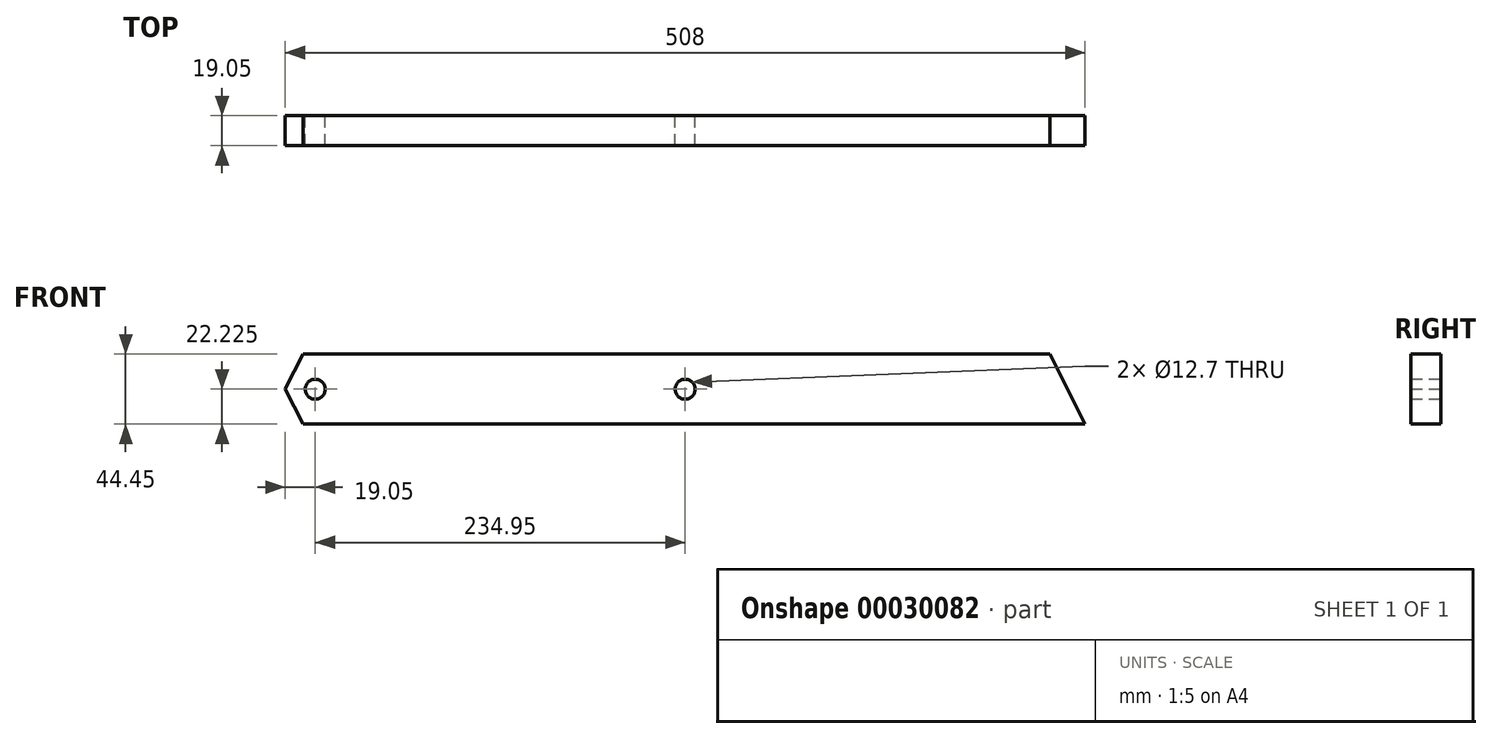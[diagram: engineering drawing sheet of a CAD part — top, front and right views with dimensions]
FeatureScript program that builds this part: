
annotation { "Feature Type Name" : "Feature", "Feature Type Description" : "" }
export const myFeature = defineFeature(function(context is Context, id is Id, definition is map)
    precondition{}
    {
        {
            var Q0;
            Q0=qCreatedBy(makeId("Front.planeOp"),FACE);
            var sketch = newSketch(context, id + "F0", { "sketchPlane" : qUnion([Q0])});
            skLineSegment(sketch, "E0", {"start": v(19.05, 0) * mm, "end": v(508, 0) * mm});
            skLineSegment(sketch, "E1", {"start": v(485.78, 44.45) * mm, "end": v(19.05, 44.45) * mm});
            skLineSegment(sketch, "E2", {"start": v(508, 0) * mm, "end": v(485.78, 44.45) * mm});
            skPoint(sketch, "E3.end.orphan", {"position": v(508, 44.45) * mm});
            skPoint(sketch, "E4.orphan", {"position": v(0, 44.45) * mm});
            skPoint(sketch, "E5.orphan", {"position": v(0, 0) * mm});
            skCircle(sketch, "E6", {"center": v(19.05, 22.23) * mm, "radius": 6.35 * mm});
            skLineSegment(sketch, "E7", {"start": v(0, 22.23) * mm, "end": v(25.4, 22.23) * mm});
            skCircle(sketch, "E8", {"center": v(254, 22.23) * mm, "radius": 6.35 * mm});
            skLineSegment(sketch, "E9.trimOffspring", {"start": v(247.65, 22.23) * mm, "end": v(254, 22.23) * mm});
            skPoint(sketch, "E10.orphan", {"position": v(12.7, 44.45) * mm});
            skLineSegment(sketch, "E11", {"start": v(19.05, 44.45) * mm, "end": v(0, 44.45) * mm});
            skLineSegment(sketch, "E12", {"start": v(0, 22.23) * mm, "end": v(0, 44.45) * mm});
            skLineSegment(sketch, "E13", {"start": v(0, 22.23) * mm, "end": v(0, 0) * mm});
            skLineSegment(sketch, "E14", {"start": v(19.05, 0) * mm, "end": v(0, 0) * mm});
            skLineSegment(sketch, "E15", {"start": v(0, 22.23) * mm, "end": v(11.32, 44.45) * mm});
            skLineSegment(sketch, "E16", {"start": v(11.32, 44.45) * mm, "end": v(0, 22.23) * mm});
            skLineSegment(sketch, "E17", {"start": v(11.32, 0) * mm, "end": v(0, 22.23) * mm});
            skSolve(sketch);
        }
        {
            var Q0;
            Q0=makeQuery(id+"F0.imprint","IMPRINT",FACE,{"disambiguationData":[TD([[makeQuery(id+"F0.imprint","IMPRINT",EDGE,{"derivedFrom":sQuery(id+"F0.wireOp",EDGE,"E0")}),1.0]])]});
            extrude(context, id + "F1", {"entities" : qUnion([Q0]), "depth" : 19.05 * mm});
        }
    });
